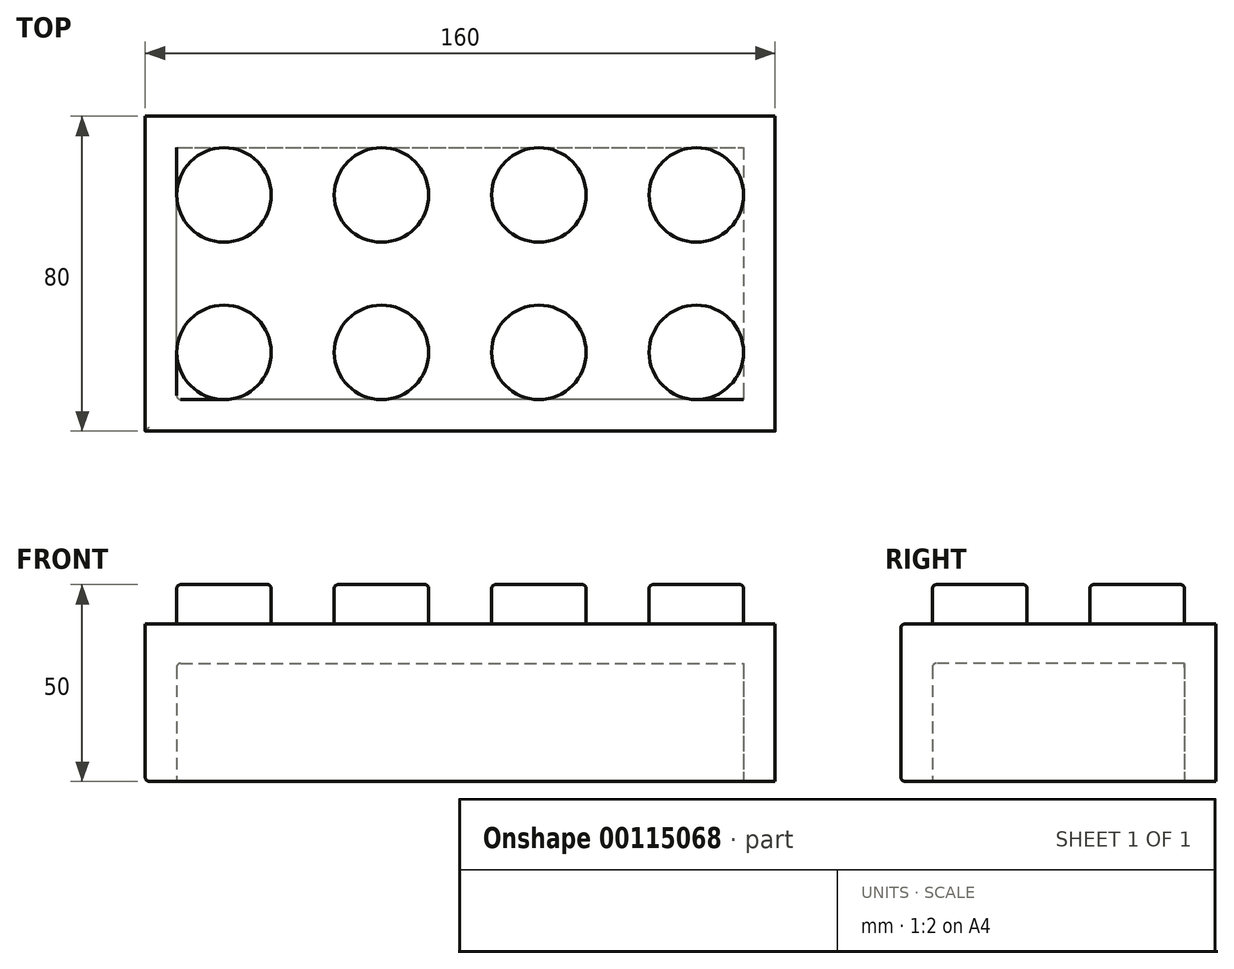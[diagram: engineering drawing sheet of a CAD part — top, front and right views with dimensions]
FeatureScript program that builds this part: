
annotation { "Feature Type Name" : "Feature", "Feature Type Description" : "" }
export const myFeature = defineFeature(function(context is Context, id is Id, definition is map)
    precondition{}
    {
        {
            var Q0;
            Q0=qCreatedBy(makeId("Top.planeOp"),FACE);
            var sketch = newSketch(context, id + "F0", { "sketchPlane" : qUnion([Q0])});
            skLineSegment(sketch, "E0.bottom", {"start": v(-70.6, 55.3) * mm, "end": v(89.4, 55.3) * mm});
            skLineSegment(sketch, "E0.top", {"start": v(-70.6, -24.7) * mm, "end": v(89.4, -24.7) * mm});
            skLineSegment(sketch, "E0.left", {"start": v(-70.6, 55.3) * mm, "end": v(-70.6, -24.7) * mm});
            skLineSegment(sketch, "E0.right", {"start": v(89.4, 55.3) * mm, "end": v(89.4, -24.7) * mm});
            skSolve(sketch);
        }
        {
            var Q0;
            Q0 = qSketchRegion(id + "F0", true);
            extrude(context, id + "F1", {"entities" : qUnion([Q0]), "depth" : 40 * mm});
        }
        {
            var Q0;
            Q0=makeQuery(id+"F1.opExtrude","CAP_FACE",FACE,{"disambiguationData":[OSD([sQuery(id+"F0.wireOp",EDGE,"E0.bottom"),sQuery(id+"F0.wireOp",EDGE,"E0.top"),sQuery(id+"F0.wireOp",EDGE,"E0.left"),sQuery(id+"F0.wireOp",EDGE,"E0.right")])],"isStart":true});
            var sketch = newSketch(context, id + "F2", { "sketchPlane" : qUnion([Q0])});
            skLineSegment(sketch, "E1.0", {"start": v(-62.6, -47.3) * mm, "end": v(81.4, -47.3) * mm});
            skLineSegment(sketch, "E1.1", {"start": v(-62.6, 16.7) * mm, "end": v(-62.6, -47.3) * mm});
            skLineSegment(sketch, "E1.2", {"start": v(81.4, 16.7) * mm, "end": v(-62.6, 16.7) * mm});
            skLineSegment(sketch, "E1.3", {"start": v(81.4, -47.3) * mm, "end": v(81.4, 16.7) * mm});
            skSolve(sketch);
        }
        {
            var Q0;
            Q0 = qSketchRegion(id + "F2", true);
            extrude(context, id + "F3", {"entities" : qUnion([Q0]), "operationType" : NewBodyOperationType.REMOVE, "oppositeDirection" : true, "depth" : 30 * mm});
        }
        {
            var Q0;
            Q0=makeQuery(id+"F1.opExtrude","CAP_FACE",FACE,{"disambiguationData":[OSD([sQuery(id+"F0.wireOp",EDGE,"E0.bottom"),sQuery(id+"F0.wireOp",EDGE,"E0.top"),sQuery(id+"F0.wireOp",EDGE,"E0.left"),sQuery(id+"F0.wireOp",EDGE,"E0.right")])],"isStart":false});
            var sketch = newSketch(context, id + "F4", { "sketchPlane" : qUnion([Q0])});
            skCircle(sketch, "E2", {"center": v(-50.6, 35.3) * mm, "radius": 12 * mm});
            skCircle(sketch, "E3.0.1.0", {"center": v(-50.6, -4.7) * mm, "radius": 12 * mm});
            skCircle(sketch, "E3.1.0.0", {"center": v(-10.6, 35.3) * mm, "radius": 12 * mm});
            skCircle(sketch, "E3.1.1.0", {"center": v(-10.6, -4.7) * mm, "radius": 12 * mm});
            skCircle(sketch, "E3.2.0.0", {"center": v(29.4, 35.3) * mm, "radius": 12 * mm});
            skCircle(sketch, "E3.2.1.0", {"center": v(29.4, -4.7) * mm, "radius": 12 * mm});
            skCircle(sketch, "E3.3.0.0", {"center": v(69.4, 35.3) * mm, "radius": 12 * mm});
            skCircle(sketch, "E3.3.1.0", {"center": v(69.4, -4.7) * mm, "radius": 12 * mm});
            skLineSegment(sketch, "E3.direction1", {"start": v(-50.6, 35.3) * mm, "end": v(-10.6, 35.3) * mm, "construction": true});
            skLineSegment(sketch, "E3.direction2", {"start": v(-50.6, 35.3) * mm, "end": v(-50.6, -4.7) * mm, "construction": true});
            skSolve(sketch);
        }
        {
            var Q0;
            Q0 = qSketchRegion(id + "F4", true);
            var Q1;
            Q1 = qConstructionFilter(qBodyType(qCreatedBy(id + "F4" ,EDGE), BodyType.WIRE), ConstructionObject.NO);
            extrude(context, id + "F5", {"entities" : qUnion([Q0]), "operationType" : NewBodyOperationType.ADD, "surfaceEntities" : qUnion([Q1]), "depth" : 10 * mm});
        }
        {
            var Q0;
            Q0=makeQuery(id+"F5.opExtrude","CAP_FACE",FACE,{"disambiguationData":[OSD([sQuery(id+"F4.wireOp",EDGE,"E3.0.1.0")])],"isStart":false});
            var Q1;
            Q1=makeQuery(id+"F5.opExtrude","CAP_FACE",FACE,{"disambiguationData":[OSD([sQuery(id+"F4.wireOp",EDGE,"E2")])],"isStart":false});
            var Q2;
            Q2=makeQuery(id+"F5.opExtrude","CAP_FACE",FACE,{"disambiguationData":[OSD([sQuery(id+"F4.wireOp",EDGE,"E3.1.0.0")])],"isStart":false});
            var Q3;
            Q3=makeQuery(id+"F5.opExtrude","CAP_FACE",FACE,{"disambiguationData":[OSD([sQuery(id+"F4.wireOp",EDGE,"E3.1.1.0")])],"isStart":false});
            var Q4;
            Q4=makeQuery(id+"F1.opExtrude","CAP_EDGE",EDGE,{"disambiguationData":[OSD([sQuery(id+"F0.wireOp",EDGE,"E0.top")])],"isStart":true});
            var Q5;
            Q5=makeQuery(id+"F1.opExtrude","CAP_EDGE",EDGE,{"disambiguationData":[OSD([sQuery(id+"F0.wireOp",EDGE,"E0.top")])],"isStart":false});
            var Q6;
            Q6=makeQuery(id+"F3.boolean.opBoolean","COPY",EDGE,{"derivedFrom":makeQuery(id+"F3.opExtrude","SWEPT_EDGE",EDGE,{"disambiguationData":[OSD([sQuery(id+"F2.wireOp",EDGE,"E1.1"),sQuery(id+"F2.wireOp",EDGE,"E1.2")])]})});
            var Q7;
            Q7=makeQuery(id+"F3.boolean.opBoolean","COPY",EDGE,{"derivedFrom":makeQuery(id+"F3.opExtrude","CAP_EDGE",EDGE,{"disambiguationData":[OSD([sQuery(id+"F2.wireOp",EDGE,"E1.1")])],"isStart":false})});
            var Q8;
            Q8=makeQuery(id+"F3.boolean.opBoolean","COPY",EDGE,{"derivedFrom":makeQuery(id+"F3.opExtrude","CAP_EDGE",EDGE,{"disambiguationData":[OSD([sQuery(id+"F2.wireOp",EDGE,"E1.2")])],"isStart":false})});
            var Q9;
            Q9=makeQuery(id+"F1.opExtrude","CAP_EDGE",EDGE,{"disambiguationData":[OSD([sQuery(id+"F0.wireOp",EDGE,"E0.left")])],"isStart":true});
            var Q10;
            Q10=makeQuery(id+"F3.boolean.opBoolean","COPY",EDGE,{"derivedFrom":makeQuery(id+"F3.opExtrude","CAP_EDGE",EDGE,{"disambiguationData":[OSD([sQuery(id+"F2.wireOp",EDGE,"E1.1")])],"isStart":true})});
            var Q11;
            Q11=makeQuery(id+"F3.boolean.opBoolean","COPY",EDGE,{"derivedFrom":makeQuery(id+"F3.opExtrude","CAP_EDGE",EDGE,{"disambiguationData":[OSD([sQuery(id+"F2.wireOp",EDGE,"E1.2")])],"isStart":true})});
            var Q12;
            Q12=makeQuery(id+"F5.opExtrude","CAP_FACE",FACE,{"disambiguationData":[OSD([sQuery(id+"F4.wireOp",EDGE,"E3.2.1.0")])],"isStart":false});
            var Q13;
            Q13=makeQuery(id+"F5.opExtrude","CAP_FACE",FACE,{"disambiguationData":[OSD([sQuery(id+"F4.wireOp",EDGE,"E3.0.1.0")])],"isStart":false});
            var Q14;
            Q14=makeQuery(id+"F5.opExtrude","CAP_FACE",FACE,{"disambiguationData":[OSD([sQuery(id+"F4.wireOp",EDGE,"E2")])],"isStart":false});
            var Q15;
            Q15=makeQuery(id+"F5.opExtrude","CAP_FACE",FACE,{"disambiguationData":[OSD([sQuery(id+"F4.wireOp",EDGE,"E3.1.0.0")])],"isStart":false});
            var Q16;
            Q16=makeQuery(id+"F5.opExtrude","CAP_FACE",FACE,{"disambiguationData":[OSD([sQuery(id+"F4.wireOp",EDGE,"E3.1.1.0")])],"isStart":false});
            var Q17;
            Q17=makeQuery(id+"F5.opExtrude","CAP_FACE",FACE,{"disambiguationData":[OSD([sQuery(id+"F4.wireOp",EDGE,"E3.2.1.0")])],"isStart":false});
            var Q18;
            Q18=makeQuery(id+"F5.opExtrude","CAP_FACE",FACE,{"disambiguationData":[OSD([sQuery(id+"F4.wireOp",EDGE,"E3.3.1.0")])],"isStart":false});
            var Q19;
            Q19=makeQuery(id+"F5.opExtrude","CAP_FACE",FACE,{"disambiguationData":[OSD([sQuery(id+"F4.wireOp",EDGE,"E3.3.0.0")])],"isStart":false});
            var Q20;
            Q20=makeQuery(id+"F5.opExtrude","CAP_FACE",FACE,{"disambiguationData":[OSD([sQuery(id+"F4.wireOp",EDGE,"E3.2.0.0")])],"isStart":false});
            fillet(context, id + "F6", {"entities" : qUnion([Q0, Q1, Q2, Q3, Q4, Q5, Q6, Q7, Q8, Q9, Q10, Q11, Q12, Q13, Q14, Q15, Q16, Q17, Q18, Q19, Q20]), "radius" : 1 * mm, "tangentPropagation" : true, "allowEdgeOverflow" : false});
        }
    });
